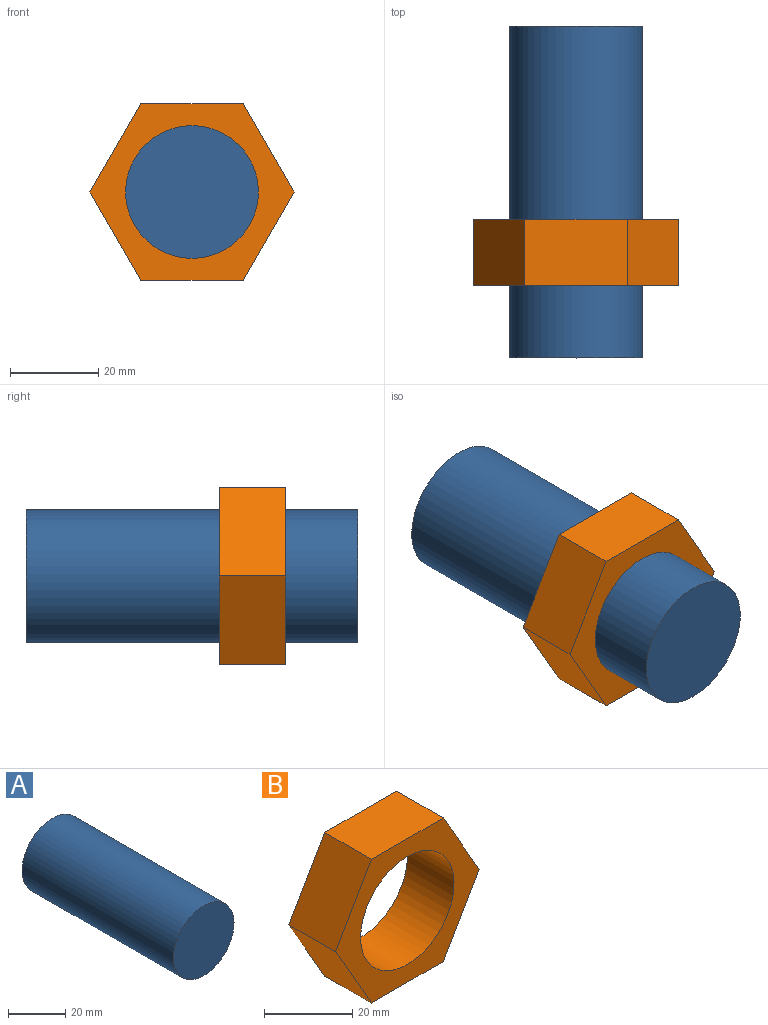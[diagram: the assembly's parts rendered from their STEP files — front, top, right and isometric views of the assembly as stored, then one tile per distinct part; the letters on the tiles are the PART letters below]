
ASSEMBLY  parts=2 mates=1
PART A: 3 faces, bbox 30x75x30 mm
  f0: cylinder r=15mm len=75mm, axis (0,1,0), area 7068.6mm2, adj f1,f2
  f1: plane 30x30mm, normal (0,-1,0), area 706.9mm2, adj f0
  f2: plane 30x30mm, normal (0,1,0), area 706.9mm2, adj f0
PART B: 9 faces, bbox 46.1x15x39.9 mm
  f0: plane 19.97x15mm, normal (-0.87,0,-0.5), area 345.9mm2, adj f1,f6,f7,f8
  f1: plane 23.06x15mm, normal (0,0,-1), area 345.9mm2, adj f0,f2,f7,f8
  f2: plane 19.97x15mm, normal (0.87,0,-0.5), area 345.9mm2, adj f1,f3,f7,f8
  f3: plane 19.97x15mm, normal (0.87,0,0.5), area 345.9mm2, adj f2,f4,f7,f8
  f4: plane 23.06x15mm, normal (0,0,1), area 345.9mm2, adj f3,f6,f7,f8
  f5: cylinder r=15mm len=30mm, axis (0,1,0), area 1413.7mm2, adj f7,f8
  f6: plane 19.97x15mm, normal (-0.87,0,0.5), area 345.9mm2, adj f0,f4,f7,f8
  f7: plane 46.12x39.94mm, normal (0,-1,0), area 674.9mm2, adj f0,f1,f2,f3,f4,f5,f6
  f8: plane 46.12x39.94mm, normal (0,1,0), area 674.9mm2, adj f0,f1,f2,f3,f4,f5,f6
PLACE A t=(-41.81,31.5,-17.79)mm
PLACE B t=(-41.81,-12.15,-17.79)mm
MATE slider A.f0 <-> B.f5  axis (0,-1,0) through (-41.81,-43.5,-17.79)mm
